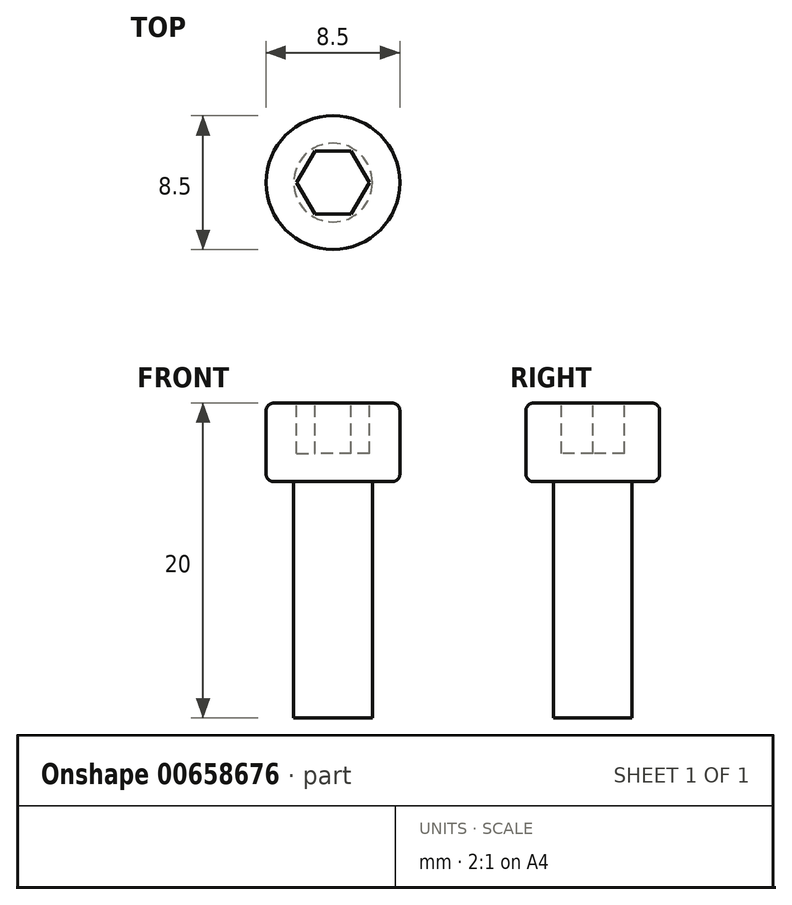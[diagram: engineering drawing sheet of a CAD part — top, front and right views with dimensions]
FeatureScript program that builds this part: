
annotation { "Feature Type Name" : "Feature", "Feature Type Description" : "" }
export const myFeature = defineFeature(function(context is Context, id is Id, definition is map)
    precondition{}
    {
        {
            var Q0;
            Q0=qCreatedBy(makeId("Top.planeOp"),FACE);
            var sketch = newSketch(context, id + "F0", { "sketchPlane" : qUnion([Q0])});
            skCircle(sketch, "E0", {"center": v(0, 0) * mm, "radius": 4.25 * mm});
            skSolve(sketch);
        }
        {
            var Q0;
            Q0=makeQuery(id+"F0.imprint","IMPRINT",FACE,{"disambiguationData":[TD([[makeQuery(id+"F0.imprint","IMPRINT",EDGE,{"derivedFrom":sQuery(id+"F0.wireOp",EDGE,"E0")}),1.0]])]});
            extrude(context, id + "F1", {"entities" : qUnion([Q0]), "depth" : 5 * mm});
        }
        {
            var Q0;
            Q0=makeQuery(id+"F1.opExtrude","CAP_FACE",FACE,{"disambiguationData":[OSD([sQuery(id+"F0.wireOp",EDGE,"E0")])],"isStart":true});
            var sketch = newSketch(context, id + "F2", { "sketchPlane" : qUnion([Q0])});
            skCircle(sketch, "E1", {"center": v(0, 0) * mm, "radius": 2.5 * mm});
            skSolve(sketch);
        }
        {
            var Q0;
            Q0=makeQuery(id+"F2.imprint","IMPRINT",FACE,{"disambiguationData":[TD([[makeQuery(id+"F2.imprint","IMPRINT",EDGE,{"derivedFrom":sQuery(id+"F2.wireOp",EDGE,"E1")}),1.0]])]});
            extrude(context, id + "F3", {"entities" : qUnion([Q0]), "operationType" : NewBodyOperationType.ADD, "depth" : 15 * mm});
        }
        {
            var Q0;
            Q0=makeQuery(id+"F1.opExtrude","CAP_FACE",FACE,{"disambiguationData":[OSD([sQuery(id+"F0.wireOp",EDGE,"E0")])],"isStart":false});
            var sketch = newSketch(context, id + "F4", { "sketchPlane" : qUnion([Q0])});
            skCircle(sketch, "E2.cCircle", {"center": v(0, 0) * mm, "radius": 2 * mm, "construction": true});
            skLineSegment(sketch, "E2.0", {"start": v(1.15, -2) * mm, "end": v(-1.15, -2) * mm});
            skLineSegment(sketch, "E2.1", {"start": v(-1.15, -2) * mm, "end": v(-2.3, 0) * mm});
            skLineSegment(sketch, "E2.2", {"start": v(-2.3, 0) * mm, "end": v(-1.15, 2) * mm});
            skLineSegment(sketch, "E2.3", {"start": v(-1.15, 2) * mm, "end": v(1.15, 2) * mm});
            skLineSegment(sketch, "E2.4", {"start": v(1.15, 2) * mm, "end": v(2.3, 0) * mm});
            skLineSegment(sketch, "E2.5", {"start": v(2.3, 0) * mm, "end": v(1.15, -2) * mm});
            skPoint(sketch, "E2.0.midPoint", {"position": v(0, -2) * mm});
            skSolve(sketch);
        }
        {
            var Q0;
            Q0=makeQuery(id+"F4.imprint","IMPRINT",FACE,{"disambiguationData":[TD([[makeQuery(id+"F4.imprint","IMPRINT",EDGE,{"derivedFrom":sQuery(id+"F4.wireOp",EDGE,"E2.0")}),-1.0]])]});
            extrude(context, id + "F5", {"entities" : qUnion([Q0]), "operationType" : NewBodyOperationType.REMOVE, "oppositeDirection" : true, "depth" : 3.2 * mm});
        }
        {
            var Q0;
            Q0=makeQuery(id+"F1.opExtrude","CAP_EDGE",EDGE,{"disambiguationData":[OSD([sQuery(id+"F0.wireOp",EDGE,"E0")])],"isStart":false});
            var Q1;
            Q1=makeQuery(id+"F1.opExtrude","CAP_EDGE",EDGE,{"disambiguationData":[OSD([sQuery(id+"F0.wireOp",EDGE,"E0")])],"isStart":true});
            fillet(context, id + "F6", {"entities" : qUnion([Q0, Q1]), "radius" : .5 * mm, "tangentPropagation" : true, "allowEdgeOverflow" : false});
        }
    });
